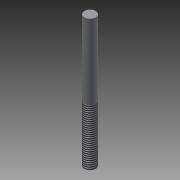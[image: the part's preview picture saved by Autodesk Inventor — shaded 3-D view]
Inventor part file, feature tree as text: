
AUTODESK INVENTOR PART (.ipt)
format: ipt  version: 2015 (Build 190159000, 159)  size: 73,216 bytes
history: native  units: mm
features: extrude x1, thread x1, sketch x1
ambient origin geometry x8: Origin, YZ Plane, XZ Plane, XY Plane, X Axis, Y Axis, Z Axis, Center Point
bodies: Body1 (feature_tree)
feature tree (3):
  extrude  "Extrusion3"  Depth=35.0mm TaperAngle=0.0deg
  thread  "Thread4"  [1 undecoded]
  sketch  "Sketch3"  dims[d12=3.0mm d13=35.0mm d14=0.0mm d15=15.0mm d16=0.0mm]
note: 1 required parameter value undecoded (feature->parameter linkage not recoverable at this tier; creation-order binding heuristic only, values carry confidence <= 0.55)
